FCSTD DOCUMENT  (FreeCAD 0.20R26155 (Git))
Label: C707 10M008 612 2
License: All rights reserved
LicenseURL: http://en.wikipedia.org/wiki/All_rights_reserved
objects: Sketcher::SketchObject×3
note: 3 computed .brp shape members not serialized (recipe doc carries the construction recipe); baked Part::Feature solids carry a one-line shape summary decoded from their .brp

FEATURE [Sketcher::SketchObject] Sketch  label="F_Silks_0.16"
  FullyConstrained = false
  MapMode = 5
  sketch-geometry (118):
    g0: LineSegment StartX=-3.32 StartY=-3.84 StartZ=0 EndX=-2.42 EndY=-3.84 EndZ=0
    g1: LineSegment StartX=-2.42 StartY=-3.84 StartZ=0 EndX=-2.42 EndY=-2.74 EndZ=0
    g2: LineSegment StartX=-2.42 StartY=-2.74 StartZ=0 EndX=-3.32 EndY=-2.74 EndZ=0
    g3: LineSegment StartX=-3.32 StartY=-2.74 StartZ=0 EndX=-3.32 EndY=-3.84 EndZ=0
    g4: LineSegment StartX=-3.32 StartY=-2.34 StartZ=0 EndX=-2.42 EndY=-2.34 EndZ=0
    g5: LineSegment StartX=-2.42 StartY=-2.34 StartZ=0 EndX=-2.42 EndY=-0.2 EndZ=0
    g6: LineSegment StartX=-2.42 StartY=-0.2 StartZ=0 EndX=-3.32 EndY=-0.2 EndZ=0
    g7: LineSegment StartX=-3.32 StartY=-0.2 StartZ=0 EndX=-3.32 EndY=-2.34 EndZ=0
    g8: LineSegment StartX=-3.32 StartY=-3.84 StartZ=0 EndX=-3.32 EndY=15.0884 EndZ=0
    g9: LineSegment StartX=2.42 StartY=-3.84 StartZ=0 EndX=3.32 EndY=-3.84 EndZ=0
    g10: LineSegment StartX=3.32 StartY=-3.84 StartZ=0 EndX=3.32 EndY=-2.74 EndZ=0
    g11: LineSegment StartX=3.32 StartY=-2.74 StartZ=0 EndX=2.42 EndY=-2.74 EndZ=0
    g12: LineSegment StartX=2.42 StartY=-2.74 StartZ=0 EndX=2.42 EndY=-3.84 EndZ=0
    g13: LineSegment StartX=2.42 StartY=-2.34 StartZ=0 EndX=3.32 EndY=-2.34 EndZ=0
    g14: LineSegment StartX=3.32 StartY=-2.34 StartZ=0 EndX=3.32 EndY=-0.2 EndZ=0
    g15: LineSegment StartX=3.32 StartY=-0.2 StartZ=0 EndX=2.42 EndY=-0.2 EndZ=0
    g16: LineSegment StartX=2.42 StartY=-0.2 StartZ=0 EndX=2.42 EndY=-2.34 EndZ=0
    g17: LineSegment StartX=-3.32 StartY=0.2 StartZ=0 EndX=-2.42 EndY=0.2 EndZ=0
    g18: LineSegment StartX=-2.42 StartY=0.2 StartZ=0 EndX=-2.42 EndY=2.34 EndZ=0
    g19: LineSegment StartX=-2.42 StartY=2.34 StartZ=0 EndX=-3.32 EndY=2.34 EndZ=0
    g20: LineSegment StartX=-3.32 StartY=2.34 StartZ=0 EndX=-3.32 EndY=0.2 EndZ=0
    g21: LineSegment StartX=2.42 StartY=0.2 StartZ=0 EndX=3.32 EndY=0.2 EndZ=0
    g22: LineSegment StartX=3.32 StartY=0.2 StartZ=0 EndX=3.32 EndY=2.34 EndZ=0
    g23: LineSegment StartX=3.32 StartY=2.34 StartZ=0 EndX=2.42 EndY=2.34 EndZ=0
    g24: LineSegment StartX=2.42 StartY=2.34 StartZ=0 EndX=2.42 EndY=0.2 EndZ=0
    g25: LineSegment StartX=2.42 StartY=-3.84 StartZ=0 EndX=2.42 EndY=14.9394 EndZ=0
    g26: LineSegment StartX=-3.32 StartY=2.74 StartZ=0 EndX=-2.42 EndY=2.74 EndZ=0
    g27: LineSegment StartX=-2.42 StartY=2.74 StartZ=0 EndX=-2.42 EndY=3.84 EndZ=0
    g28: LineSegment StartX=-2.42 StartY=3.84 StartZ=0 EndX=-3.32 EndY=3.84 EndZ=0
    g29: LineSegment StartX=-3.32 StartY=3.84 StartZ=0 EndX=-3.32 EndY=2.74 EndZ=0
    g30: LineSegment StartX=2.42 StartY=2.74 StartZ=0 EndX=3.32 EndY=2.74 EndZ=0
    g31: LineSegment StartX=3.32 StartY=2.74 StartZ=0 EndX=3.32 EndY=3.84 EndZ=0
    g32: LineSegment StartX=3.32 StartY=3.84 StartZ=0 EndX=2.42 EndY=3.84 EndZ=0
    g33: LineSegment StartX=2.42 StartY=3.84 StartZ=0 EndX=2.42 EndY=2.74 EndZ=0
    g34: LineSegment StartX=-4.32 StartY=5.13365 StartZ=0 EndX=-4.32 EndY=14.1961 EndZ=0
    g35: LineSegment StartX=3.62 StartY=5.28538 StartZ=0 EndX=3.62 EndY=13.9122 EndZ=0
    g36: LineSegment StartX=-4.32 StartY=-3.19 StartZ=0 EndX=-3.62 EndY=-3.19 EndZ=0
    g37: LineSegment StartX=-3.62 StartY=-3.19 StartZ=0 EndX=-3.62 EndY=-1.89 EndZ=0
    g38: LineSegment StartX=-3.62 StartY=-1.89 StartZ=0 EndX=-4.32 EndY=-1.89 EndZ=0
    g39: LineSegment StartX=-4.32 StartY=-1.89 StartZ=0 EndX=-4.32 EndY=-3.19 EndZ=0
    g40: LineSegment StartX=-4.32 StartY=-0.65 StartZ=0 EndX=-3.62 EndY=-0.65 EndZ=0
    g41: LineSegment StartX=-3.62 StartY=-0.65 StartZ=0 EndX=-3.62 EndY=0.65 EndZ=0
    g42: LineSegment StartX=-3.62 StartY=0.65 StartZ=0 EndX=-4.32 EndY=0.65 EndZ=0
    g43: LineSegment StartX=-4.32 StartY=0.65 StartZ=0 EndX=-4.32 EndY=-0.65 EndZ=0
    g44: LineSegment StartX=-4.32 StartY=1.89 StartZ=0 EndX=-3.62 EndY=1.89 EndZ=0
    g45: LineSegment StartX=-3.62 StartY=1.89 StartZ=0 EndX=-3.62 EndY=3.19 EndZ=0
    g46: LineSegment StartX=-3.62 StartY=3.19 StartZ=0 EndX=-4.32 EndY=3.19 EndZ=0
    g47: LineSegment StartX=-4.32 StartY=3.19 StartZ=0 EndX=-4.32 EndY=1.89 EndZ=0
    g48: LineSegment StartX=3.62 StartY=1.89 StartZ=0 EndX=4.32 EndY=1.89 EndZ=0
    g49: LineSegment StartX=4.32 StartY=1.89 StartZ=0 EndX=4.32 EndY=3.19 EndZ=0
    g50: LineSegment StartX=4.32 StartY=3.19 StartZ=0 EndX=3.62 EndY=3.19 EndZ=0
    g51: LineSegment StartX=3.62 StartY=3.19 StartZ=0 EndX=3.62 EndY=1.89 EndZ=0
    g52: LineSegment StartX=3.62 StartY=-0.65 StartZ=0 EndX=4.32 EndY=-0.65 EndZ=0
    g53: LineSegment StartX=4.32 StartY=-0.65 StartZ=0 EndX=4.32 EndY=0.65 EndZ=0
    g54: LineSegment StartX=4.32 StartY=0.65 StartZ=0 EndX=3.62 EndY=0.65 EndZ=0
    g55: LineSegment StartX=3.62 StartY=0.65 StartZ=0 EndX=3.62 EndY=-0.65 EndZ=0
    g56: LineSegment StartX=3.62 StartY=-3.19 StartZ=0 EndX=4.32 EndY=-3.19 EndZ=0
    g57: LineSegment StartX=4.32 StartY=-3.19 StartZ=0 EndX=4.32 EndY=-1.89 EndZ=0
    g58: LineSegment StartX=4.32 StartY=-1.89 StartZ=0 EndX=3.62 EndY=-1.89 EndZ=0
    g59: LineSegment StartX=3.62 StartY=-1.89 StartZ=0 EndX=3.62 EndY=-3.19 EndZ=0
    g60: LineSegment StartX=-2.42 StartY=-2.34 StartZ=0 EndX=2.42 EndY=-2.34 EndZ=0
    g61: LineSegment StartX=-2.42 StartY=0.2 StartZ=0 EndX=2.42 EndY=0.2 EndZ=0
    g62: LineSegment StartX=-2.42 StartY=2.74 StartZ=0 EndX=2.42 EndY=2.74 EndZ=0
    g63: LineSegment StartX=-2.42 StartY=-3.84 StartZ=0 EndX=2.42 EndY=-3.84 EndZ=0
    g64: LineSegment StartX=-3.62 StartY=-3.19 StartZ=0 EndX=3.62 EndY=-3.19 EndZ=0
    g65: LineSegment StartX=-3.62 StartY=-0.65 StartZ=0 EndX=3.62 EndY=-0.65 EndZ=0
    g66: LineSegment StartX=-3.62 StartY=1.89 StartZ=0 EndX=3.62 EndY=1.89 EndZ=0
    g67: LineSegment StartX=-0.9 StartY=-3.29 StartZ=0 EndX=-0.34 EndY=-3.29 EndZ=0
    g68: LineSegment StartX=-0.34 StartY=-3.29 StartZ=0 EndX=-0.34 EndY=-2.95 EndZ=0
    g69: LineSegment StartX=-0.34 StartY=-2.95 StartZ=0 EndX=-0.9 EndY=-2.95 EndZ=0
    g70: LineSegment StartX=-0.9 StartY=-2.95 StartZ=0 EndX=-0.9 EndY=-3.29 EndZ=0
    g71: LineSegment StartX=0.34 StartY=-3.29 StartZ=0 EndX=0.9 EndY=-3.29 EndZ=0
    g72: LineSegment StartX=0.9 StartY=-3.29 StartZ=0 EndX=0.9 EndY=-2.95 EndZ=0
    g73: LineSegment StartX=0.9 StartY=-2.95 StartZ=0 EndX=0.34 EndY=-2.95 EndZ=0
    g74: LineSegment StartX=0.34 StartY=-2.95 StartZ=0 EndX=0.34 EndY=-3.29 EndZ=0
    g75: LineSegment StartX=0.04 StartY=-2.31 StartZ=0 EndX=0.79 EndY=-2.31 EndZ=0
    g76: LineSegment StartX=0.79 StartY=-2.31 StartZ=0 EndX=0.79 EndY=-2.81 EndZ=0
    g77: LineSegment StartX=0.79 StartY=-2.81 StartZ=0 EndX=0.04 EndY=-2.81 EndZ=0
    g78: LineSegment StartX=0.04 StartY=-2.81 StartZ=0 EndX=0.04 EndY=-2.31 EndZ=0
    g79: LineSegment StartX=-0.79 StartY=-1.66 StartZ=0 EndX=-0.04 EndY=-1.66 EndZ=0
    g80: LineSegment StartX=-0.04 StartY=-1.66 StartZ=0 EndX=-0.04 EndY=-2.16 EndZ=0
    g81: LineSegment StartX=-0.04 StartY=-2.16 StartZ=0 EndX=-0.79 EndY=-2.16 EndZ=0
    g82: LineSegment StartX=-0.79 StartY=-2.16 StartZ=0 EndX=-0.79 EndY=-1.66 EndZ=0
    g83: LineSegment StartX=0.04 StartY=-1.07 StartZ=0 EndX=0.79 EndY=-1.07 EndZ=0
    g84: LineSegment StartX=0.79 StartY=-1.07 StartZ=0 EndX=0.79 EndY=-0.57 EndZ=0
    g85: LineSegment StartX=0.79 StartY=-0.57 StartZ=0 EndX=0.04 EndY=-0.57 EndZ=0
    g86: LineSegment StartX=0.04 StartY=-0.57 StartZ=0 EndX=0.04 EndY=-1.07 EndZ=0
    g87: LineSegment StartX=-0.79 StartY=1.07 StartZ=0 EndX=-0.04 EndY=1.07 EndZ=0
    g88: LineSegment StartX=-0.04 StartY=1.07 StartZ=0 EndX=-0.04 EndY=0.57 EndZ=0
    g89: LineSegment StartX=-0.04 StartY=0.57 StartZ=0 EndX=-0.79 EndY=0.57 EndZ=0
    g90: LineSegment StartX=-0.79 StartY=0.57 StartZ=0 EndX=-0.79 EndY=1.07 EndZ=0
    g91: LineSegment StartX=0.04 StartY=1.66 StartZ=0 EndX=0.79 EndY=1.66 EndZ=0
    g92: LineSegment StartX=0.79 StartY=1.66 StartZ=0 EndX=0.79 EndY=2.16 EndZ=0
    g93: LineSegment StartX=0.79 StartY=2.16 StartZ=0 EndX=0.04 EndY=2.16 EndZ=0
    g94: LineSegment StartX=0.04 StartY=2.16 StartZ=0 EndX=0.04 EndY=1.66 EndZ=0
    g95: LineSegment StartX=-0.79 StartY=2.81 StartZ=0 EndX=-0.04 EndY=2.81 EndZ=0
    g96: LineSegment StartX=-0.04 StartY=2.81 StartZ=0 EndX=-0.04 EndY=2.31 EndZ=0
    g97: LineSegment StartX=-0.04 StartY=2.31 StartZ=0 EndX=-0.79 EndY=2.31 EndZ=0
    g98: LineSegment StartX=-0.79 StartY=2.31 StartZ=0 EndX=-0.79 EndY=2.81 EndZ=0
    g99: LineSegment StartX=0.34 StartY=3.29 StartZ=0 EndX=0.9 EndY=3.29 EndZ=0
    g100: LineSegment StartX=0.9 StartY=3.29 StartZ=0 EndX=0.9 EndY=2.95 EndZ=0
    g101: LineSegment StartX=0.9 StartY=2.95 StartZ=0 EndX=0.34 EndY=2.95 EndZ=0
    g102: LineSegment StartX=0.34 StartY=2.95 StartZ=0 EndX=0.34 EndY=3.29 EndZ=0
    g103: LineSegment StartX=-0.9 StartY=3.29 StartZ=0 EndX=-0.34 EndY=3.29 EndZ=0
    g104: LineSegment StartX=-0.34 StartY=3.29 StartZ=0 EndX=-0.34 EndY=2.95 EndZ=0
    g105: LineSegment StartX=-0.34 StartY=2.95 StartZ=0 EndX=-0.9 EndY=2.95 EndZ=0
    g106: LineSegment StartX=-0.9 StartY=2.95 StartZ=0 EndX=-0.9 EndY=3.29 EndZ=0
    g107: LineSegment StartX=-0.9 StartY=2.95 StartZ=0 EndX=-0.9 EndY=5.53187 EndZ=0
    g108: LineSegment StartX=-0.79 StartY=2.31 StartZ=0 EndX=-0.79 EndY=5.36472 EndZ=0
    g109: LineSegment StartX=0.04 StartY=1.66 StartZ=0 EndX=0.04 EndY=5.08492 EndZ=0
    g110: LineSegment StartX=0.34 StartY=2.95 StartZ=0 EndX=0.34 EndY=3.02051 EndZ=0
    g111: LineSegment StartX=-0.34 StartY=2.95 StartZ=0 EndX=0.34 EndY=2.95 EndZ=0
    g112: LineSegment StartX=-0.34 StartY=-3.29 StartZ=0 EndX=0.34 EndY=-3.29 EndZ=0
    g113: LineSegment StartX=4.32 StartY=-3.84 StartZ=0 EndX=4.32 EndY=3.84 EndZ=0
    g114: LineSegment StartX=4.32 StartY=3.84 StartZ=0 EndX=-4.32 EndY=3.84 EndZ=0
    g115: LineSegment StartX=-4.32 StartY=3.84 StartZ=0 EndX=-4.32 EndY=-3.84 EndZ=0
    g116: LineSegment StartX=-4.32 StartY=-3.84 StartZ=0 EndX=4.32 EndY=-3.84 EndZ=0
    g117: GeomPoint X=0 Y=0 Z=0
  constraints (334):
    c: Coincident(g0,g1)
    c: Coincident(g1,g2)
    c: Coincident(g2,g3)
    c: Coincident(g3,g0)
    c: Horizontal(g0)
    c: Horizontal(g2)
    c: Vertical(g1)
    c: Vertical(g3)
    c: DistanceX(g2,g2) = 0.9
    c: Coincident(g4,g5)
    c: Coincident(g5,g6)
    c: Coincident(g6,g7)
    c: Coincident(g7,g4)
    c: Horizontal(g4)
    c: Horizontal(g6)
    c: Vertical(g5)
    c: Vertical(g7)
    c: Coincident(g8,g0)
    c: Vertical(g8)
    c: PointOnObject(g4,g8)
    c: DistanceY(g0,g4) = 1.5
    c: Coincident(g9,g10)
    c: Coincident(g10,g11)
    c: Coincident(g11,g12)
    c: Coincident(g12,g9)
    c: Horizontal(g9)
    c: Horizontal(g11)
    c: Vertical(g10)
    c: Vertical(g12)
    c: Coincident(g13,g14)
    c: Coincident(g14,g15)
    c: Coincident(g15,g16)
    c: Coincident(g16,g13)
    c: Horizontal(g13)
    c: Horizontal(g15)
    c: Vertical(g14)
    c: Vertical(g16)
    c: Coincident(g17,g18)
    c: Coincident(g18,g19)
    c: Coincident(g19,g20)
    c: Coincident(g20,g17)
    c: Horizontal(g17)
    c: Horizontal(g19)
    c: Vertical(g18)
    c: Vertical(g20)
    c: PointOnObject(g17,g8)
    c: Coincident(g21,g22)
    c: Coincident(g22,g23)
    c: Coincident(g23,g24)
    c: Coincident(g24,g21)
    c: Horizontal(g21)
    c: Horizontal(g23)
    c: Vertical(g22)
    c: Vertical(g24)
    c: Coincident(g25,g9)
    c: Vertical(g25)
    c: PointOnObject(g23,g25)
    c: PointOnObject(g15,g25)
    c: DistanceY(g0,g17) = 4.04
    c: DistanceX(g8,g25) = 5.74
    c: Coincident(g26,g27)
    c: Coincident(g27,g28)
    c: Coincident(g28,g29)
    c: Coincident(g29,g26)
    c: Horizontal(g26)
    c: Horizontal(g28)
    c: Vertical(g27)
    c: Vertical(g29)
    c: PointOnObject(g26,g8)
    c: Coincident(g30,g31)
    c: Coincident(g31,g32)
    c: Coincident(g32,g33)
    c: Coincident(g33,g30)
    c: Horizontal(g30)
    c: Horizontal(g32)
    c: Vertical(g31)
    c: Vertical(g33)
    c: PointOnObject(g30,g25)
    c: Equal(g2,g6)
    c: Equal(g6,g19)
    c: Equal(g19,g28)
    c: Equal(g28,g32)
    c: Equal(g32,g23)
    c: Equal(g23,g15)
    c: Equal(g15,g11)
    c: Equal(g5,g18)
    c: Equal(g18,g24)
    c: Equal(g24,g16)
    c: DistanceY(g7,g7) = 2.14
    c: Equal(g1,g12)
    c: Equal(g12,g33)
    c: Equal(g33,g27)
    c: Vertical(g34)
    c: Vertical(g35)
    c: Coincident(g36,g37)
    c: Coincident(g37,g38)
    c: Coincident(g38,g39)
    c: Coincident(g39,g36)
    c: Horizontal(g36)
    c: Horizontal(g38)
    c: Vertical(g37)
    c: Vertical(g39)
    c: PointOnObject(g36,g34)
    c: Coincident(g40,g41)
    c: Coincident(g41,g42)
    c: Coincident(g42,g43)
    c: Coincident(g43,g40)
    c: Horizontal(g40)
    c: Horizontal(g42)
    c: Vertical(g41)
    c: Vertical(g43)
    c: PointOnObject(g40,g34)
    c: Coincident(g44,g45)
    c: Coincident(g45,g46)
    c: Coincident(g46,g47)
    c: Coincident(g47,g44)
    c: Horizontal(g44)
    c: Horizontal(g46)
    c: Vertical(g45)
    c: Vertical(g47)
    c: PointOnObject(g44,g34)
    c: Coincident(g48,g49)
    c: Coincident(g49,g50)
    c: Coincident(g50,g51)
    c: Coincident(g51,g48)
    c: Horizontal(g48)
    c: Horizontal(g50)
    c: Vertical(g49)
    c: Vertical(g51)
    c: PointOnObject(g48,g35)
    c: Coincident(g52,g53)
    c: Coincident(g53,g54)
    c: Coincident(g54,g55)
    c: Coincident(g55,g52)
    c: Horizontal(g52)
    c: Horizontal(g54)
    c: Vertical(g53)
    c: Vertical(g55)
    c: PointOnObject(g52,g35)
    c: Coincident(g56,g57)
    c: Coincident(g57,g58)
    c: Coincident(g58,g59)
    c: Coincident(g59,g56)
    c: Horizontal(g56)
    c: Horizontal(g58)
    c: Vertical(g57)
    c: Vertical(g59)
    c: PointOnObject(g56,g35)
    c: DistanceX(g34,g8) = 1
    c: Equal(g38,g42)
    c: Equal(g42,g46)
    c: Equal(g46,g50)
    c: Equal(g50,g54)
    c: Equal(g54,g56)
    c: Equal(g41,g45)
    c: Equal(g45,g37)
    c: Equal(g37,g57)
    c: Equal(g57,g53)
    c: Equal(g53,g49)
    c: DistanceX(g50,g50) = 0.7
    c: DistanceY(g49,g49) = 1.3
    c: Coincident(g60,g4)
    c: Coincident(g60,g13)
    c: Horizontal(g60)
    c: Coincident(g61,g17)
    c: Coincident(g61,g21)
    c: Horizontal(g61)
    c: Coincident(g62,g26)
    c: Coincident(g62,g30)
    c: Horizontal(g62)
    c: DistanceY(g0,g26) = 6.58
    c: DistanceY(g10,g10) = 1.1
    c: Coincident(g63,g0)
    c: Coincident(g63,g9)
    c: Horizontal(g63)
    c: Coincident(g64,g36)
    c: Coincident(g64,g56)
    c: Coincident(g65,g40)
    c: Coincident(g65,g52)
    c: Coincident(g66,g44)
    c: Coincident(g66,g48)
    c: Horizontal(g66)
    c: Horizontal(g65)
    c: Horizontal(g64)
    c: DistanceY(g0,g36) = 0.65
    c: DistanceY(g0,g40) = 3.19
    c: DistanceY(g0,g44) = 5.73
    c: DistanceX(g0,g35) = 6.94
    c: Coincident(g67,g68)
    c: Coincident(g68,g69)
    c: Coincident(g69,g70)
    c: Coincident(g70,g67)
    c: Horizontal(g67)
    c: Horizontal(g69)
    c: Vertical(g68)
    c: Vertical(g70)
    c: Coincident(g71,g72)
    c: Coincident(g72,g73)
    c: Coincident(g73,g74)
    c: Coincident(g74,g71)
    c: Horizontal(g71)
    c: Horizontal(g73)
    c: Vertical(g72)
    c: Vertical(g74)
    c: Coincident(g75,g76)
    c: Coincident(g76,g77)
    c: Coincident(g77,g78)
    c: Coincident(g78,g75)
    c: Horizontal(g75)
    c: Horizontal(g77)
    c: Vertical(g76)
    c: Vertical(g78)
    c: Coincident(g79,g80)
    c: Coincident(g80,g81)
    c: Coincident(g81,g82)
    c: Coincident(g82,g79)
    c: Horizontal(g79)
    c: Horizontal(g81)
    c: Vertical(g80)
    c: Vertical(g82)
    c: Coincident(g83,g84)
    c: Coincident(g84,g85)
    c: Coincident(g85,g86)
    c: Coincident(g86,g83)
    c: Horizontal(g83)
    c: Horizontal(g85)
    c: Vertical(g84)
    c: Vertical(g86)
    c: Coincident(g87,g88)
    c: Coincident(g88,g89)
    c: Coincident(g89,g90)
    c: Coincident(g90,g87)
    c: Horizontal(g87)
    c: Horizontal(g89)
    c: Vertical(g88)
    c: Vertical(g90)
    c: Coincident(g91,g92)
    c: Coincident(g92,g93)
    c: Coincident(g93,g94)
    c: Coincident(g94,g91)
    c: Horizontal(g91)
    c: Horizontal(g93)
    c: Vertical(g92)
    c: Vertical(g94)
    c: Coincident(g95,g96)
    c: Coincident(g96,g97)
    c: Coincident(g97,g98)
    c: Coincident(g98,g95)
    c: Horizontal(g95)
    c: Horizontal(g97)
    c: Vertical(g96)
    c: Vertical(g98)
    c: Coincident(g99,g100)
    c: Coincident(g100,g101)
    c: Coincident(g101,g102)
    c: Coincident(g102,g99)
    c: Horizontal(g99)
    c: Horizontal(g101)
    c: Vertical(g100)
    c: Vertical(g102)
    c: Coincident(g103,g104)
    c: Coincident(g104,g105)
    c: Coincident(g105,g106)
    c: Coincident(g106,g103)
    c: Horizontal(g103)
    c: Horizontal(g105)
    c: Vertical(g104)
    c: Vertical(g106)
    c: Coincident(g107,g105)
    c: Vertical(g107)
    c: Coincident(g108,g97)
    c: Vertical(g108)
    c: Coincident(g109,g91)
    c: Vertical(g109)
    c: Equal(g67,g71)
    c: Equal(g71,g105)
    c: Equal(g105,g101)
    c: Equal(g100,g104)
    c: Equal(g104,g72)
    c: Equal(g72,g68)
    c: Equal(g96,g94)
    c: Equal(g94,g88)
    c: Equal(g88,g86)
    c: Equal(g86,g80)
    c: Equal(g80,g78)
    c: Equal(g77,g81)
    c: Equal(g81,g83)
    c: Equal(g83,g89)
    c: Equal(g89,g91)
    c: Equal(g91,g97)
    c: PointOnObject(g83,g109)
    c: PointOnObject(g77,g109)
    c: PointOnObject(g87,g108)
    c: PointOnObject(g79,g108)
    c: Coincident(g110,g101)
    c: Vertical(g110)
    c: PointOnObject(g71,g110)
    c: DistanceX(g103,g103) = 0.56
    c: DistanceX(g95,g95) = 0.75
    c: DistanceY(g96,g96) = 0.5
    c: PointOnObject(g67,g107)
    c: DistanceX(g0,g107) = 2.42
    c: DistanceX(g0,g108) = 2.53
    c: DistanceX(g0,g109) = 3.36
    c: DistanceX(g0,g110) = 3.66
    c: Coincident(g111,g104)
    c: Coincident(g111,g101)
    c: Coincident(g112,g67)
    c: Coincident(g112,g71)
    c: Horizontal(g112)
    c: Horizontal(g111)
    c: DistanceY(g0,g67) = 0.55
    c: DistanceY(g0,g105) = 6.79
    c: DistanceY(g100,g100) = 0.34
    c: DistanceY(g0,g77) = 1.03
    c: DistanceY(g0,g81) = 1.68
    c: DistanceY(g0,g83) = 2.77
    c: DistanceY(g0,g89) = 4.41
    c: DistanceY(g0,g91) = 5.5
    c: DistanceY(g0,g97) = 6.15
    c: Coincident(g113,g114)
    c: Coincident(g114,g115)
    c: Coincident(g115,g116)
    c: Coincident(g116,g113)
    c: Horizontal(g114)
    c: Horizontal(g116)
    c: Vertical(g113)
    c: Vertical(g115)
    c: Symmetric(g114,g113,g117)
    c: Coincident(g117,g-1)
    c: PointOnObject(g28,g114)
    c: PointOnObject(g46,g115)
    c: PointOnObject(g48,g113)
    c: PointOnObject(g9,g116)
FEATURE [Sketcher::SketchObject] Sketch001  label="F_CrtYd_0.05"
  FullyConstrained = true
  MapMode = 5
  sketch-geometry (5):
    g0: LineSegment StartX=-4.5 StartY=-4 StartZ=0 EndX=-4.5 EndY=4 EndZ=0
    g1: LineSegment StartX=-4.5 StartY=4 StartZ=0 EndX=4.5 EndY=4 EndZ=0
    g2: LineSegment StartX=4.5 StartY=4 StartZ=0 EndX=4.5 EndY=-4 EndZ=0
    g3: LineSegment StartX=4.5 StartY=-4 StartZ=0 EndX=-4.5 EndY=-4 EndZ=0
    g4: GeomPoint X=0 Y=0 Z=0
  constraints (12):
    c: Coincident(g0,g1)
    c: Coincident(g1,g2)
    c: Coincident(g2,g3)
    c: Coincident(g3,g0)
    c: Horizontal(g1)
    c: Horizontal(g3)
    c: Vertical(g0)
    c: Vertical(g2)
    c: Symmetric(g1,g0,g4)
    c: Coincident(g4,g-1)
    c: DistanceY(g2,g2) = 8
    c: DistanceX(g1,g1) = 9
FEATURE [Sketcher::SketchObject] Sketch002  label="Pads_TH_SMD"
  FullyConstrained = false
  MapMode = 5
  sketch-geometry (118):
    g0: LineSegment StartX=-3.32 StartY=-3.84 StartZ=0 EndX=-2.42 EndY=-3.84 EndZ=0
    g1: LineSegment StartX=-2.42 StartY=-3.84 StartZ=0 EndX=-2.42 EndY=-2.74 EndZ=0
    g2: LineSegment StartX=-2.42 StartY=-2.74 StartZ=0 EndX=-3.32 EndY=-2.74 EndZ=0
    g3: LineSegment StartX=-3.32 StartY=-2.74 StartZ=0 EndX=-3.32 EndY=-3.84 EndZ=0
    g4: LineSegment StartX=-3.32 StartY=-2.34 StartZ=0 EndX=-2.42 EndY=-2.34 EndZ=0
    g5: LineSegment StartX=-2.42 StartY=-2.34 StartZ=0 EndX=-2.42 EndY=-0.2 EndZ=0
    g6: LineSegment StartX=-2.42 StartY=-0.2 StartZ=0 EndX=-3.32 EndY=-0.2 EndZ=0
    g7: LineSegment StartX=-3.32 StartY=-0.2 StartZ=0 EndX=-3.32 EndY=-2.34 EndZ=0
    g8: LineSegment StartX=-3.32 StartY=-3.84 StartZ=0 EndX=-3.32 EndY=15.0884 EndZ=0
    g9: LineSegment StartX=2.42 StartY=-3.84 StartZ=0 EndX=3.32 EndY=-3.84 EndZ=0
    g10: LineSegment StartX=3.32 StartY=-3.84 StartZ=0 EndX=3.32 EndY=-2.74 EndZ=0
    g11: LineSegment StartX=3.32 StartY=-2.74 StartZ=0 EndX=2.42 EndY=-2.74 EndZ=0
    g12: LineSegment StartX=2.42 StartY=-2.74 StartZ=0 EndX=2.42 EndY=-3.84 EndZ=0
    g13: LineSegment StartX=2.42 StartY=-2.34 StartZ=0 EndX=3.32 EndY=-2.34 EndZ=0
    g14: LineSegment StartX=3.32 StartY=-2.34 StartZ=0 EndX=3.32 EndY=-0.2 EndZ=0
    g15: LineSegment StartX=3.32 StartY=-0.2 StartZ=0 EndX=2.42 EndY=-0.2 EndZ=0
    g16: LineSegment StartX=2.42 StartY=-0.2 StartZ=0 EndX=2.42 EndY=-2.34 EndZ=0
    g17: LineSegment StartX=-3.32 StartY=0.2 StartZ=0 EndX=-2.42 EndY=0.2 EndZ=0
    g18: LineSegment StartX=-2.42 StartY=0.2 StartZ=0 EndX=-2.42 EndY=2.34 EndZ=0
    g19: LineSegment StartX=-2.42 StartY=2.34 StartZ=0 EndX=-3.32 EndY=2.34 EndZ=0
    g20: LineSegment StartX=-3.32 StartY=2.34 StartZ=0 EndX=-3.32 EndY=0.2 EndZ=0
    g21: LineSegment StartX=2.42 StartY=0.2 StartZ=0 EndX=3.32 EndY=0.2 EndZ=0
    g22: LineSegment StartX=3.32 StartY=0.2 StartZ=0 EndX=3.32 EndY=2.34 EndZ=0
    g23: LineSegment StartX=3.32 StartY=2.34 StartZ=0 EndX=2.42 EndY=2.34 EndZ=0
    g24: LineSegment StartX=2.42 StartY=2.34 StartZ=0 EndX=2.42 EndY=0.2 EndZ=0
    g25: LineSegment StartX=2.42 StartY=-3.84 StartZ=0 EndX=2.42 EndY=14.9394 EndZ=0
    g26: LineSegment StartX=-3.32 StartY=2.74 StartZ=0 EndX=-2.42 EndY=2.74 EndZ=0
    g27: LineSegment StartX=-2.42 StartY=2.74 StartZ=0 EndX=-2.42 EndY=3.84 EndZ=0
    g28: LineSegment StartX=-2.42 StartY=3.84 StartZ=0 EndX=-3.32 EndY=3.84 EndZ=0
    g29: LineSegment StartX=-3.32 StartY=3.84 StartZ=0 EndX=-3.32 EndY=2.74 EndZ=0
    g30: LineSegment StartX=2.42 StartY=2.74 StartZ=0 EndX=3.32 EndY=2.74 EndZ=0
    g31: LineSegment StartX=3.32 StartY=2.74 StartZ=0 EndX=3.32 EndY=3.84 EndZ=0
    g32: LineSegment StartX=3.32 StartY=3.84 StartZ=0 EndX=2.42 EndY=3.84 EndZ=0
    g33: LineSegment StartX=2.42 StartY=3.84 StartZ=0 EndX=2.42 EndY=2.74 EndZ=0
    g34: LineSegment StartX=-4.32 StartY=5.13365 StartZ=0 EndX=-4.32 EndY=14.1961 EndZ=0
    g35: LineSegment StartX=3.62 StartY=5.28538 StartZ=0 EndX=3.62 EndY=13.9122 EndZ=0
    g36: LineSegment StartX=-4.32 StartY=-3.19 StartZ=0 EndX=-3.62 EndY=-3.19 EndZ=0
    g37: LineSegment StartX=-3.62 StartY=-3.19 StartZ=0 EndX=-3.62 EndY=-1.89 EndZ=0
    g38: LineSegment StartX=-3.62 StartY=-1.89 StartZ=0 EndX=-4.32 EndY=-1.89 EndZ=0
    g39: LineSegment StartX=-4.32 StartY=-1.89 StartZ=0 EndX=-4.32 EndY=-3.19 EndZ=0
    g40: LineSegment StartX=-4.32 StartY=-0.65 StartZ=0 EndX=-3.62 EndY=-0.65 EndZ=0
    g41: LineSegment StartX=-3.62 StartY=-0.65 StartZ=0 EndX=-3.62 EndY=0.65 EndZ=0
    g42: LineSegment StartX=-3.62 StartY=0.65 StartZ=0 EndX=-4.32 EndY=0.65 EndZ=0
    g43: LineSegment StartX=-4.32 StartY=0.65 StartZ=0 EndX=-4.32 EndY=-0.65 EndZ=0
    g44: LineSegment StartX=-4.32 StartY=1.89 StartZ=0 EndX=-3.62 EndY=1.89 EndZ=0
    g45: LineSegment StartX=-3.62 StartY=1.89 StartZ=0 EndX=-3.62 EndY=3.19 EndZ=0
    g46: LineSegment StartX=-3.62 StartY=3.19 StartZ=0 EndX=-4.32 EndY=3.19 EndZ=0
    g47: LineSegment StartX=-4.32 StartY=3.19 StartZ=0 EndX=-4.32 EndY=1.89 EndZ=0
    g48: LineSegment StartX=3.62 StartY=1.89 StartZ=0 EndX=4.32 EndY=1.89 EndZ=0
    g49: LineSegment StartX=4.32 StartY=1.89 StartZ=0 EndX=4.32 EndY=3.19 EndZ=0
    g50: LineSegment StartX=4.32 StartY=3.19 StartZ=0 EndX=3.62 EndY=3.19 EndZ=0
    g51: LineSegment StartX=3.62 StartY=3.19 StartZ=0 EndX=3.62 EndY=1.89 EndZ=0
    g52: LineSegment StartX=3.62 StartY=-0.65 StartZ=0 EndX=4.32 EndY=-0.65 EndZ=0
    g53: LineSegment StartX=4.32 StartY=-0.65 StartZ=0 EndX=4.32 EndY=0.65 EndZ=0
    g54: LineSegment StartX=4.32 StartY=0.65 StartZ=0 EndX=3.62 EndY=0.65 EndZ=0
    g55: LineSegment StartX=3.62 StartY=0.65 StartZ=0 EndX=3.62 EndY=-0.65 EndZ=0
    g56: LineSegment StartX=3.62 StartY=-3.19 StartZ=0 EndX=4.32 EndY=-3.19 EndZ=0
    g57: LineSegment StartX=4.32 StartY=-3.19 StartZ=0 EndX=4.32 EndY=-1.89 EndZ=0
    g58: LineSegment StartX=4.32 StartY=-1.89 StartZ=0 EndX=3.62 EndY=-1.89 EndZ=0
    g59: LineSegment StartX=3.62 StartY=-1.89 StartZ=0 EndX=3.62 EndY=-3.19 EndZ=0
    g60: LineSegment StartX=-2.42 StartY=-2.34 StartZ=0 EndX=2.42 EndY=-2.34 EndZ=0
    g61: LineSegment StartX=-2.42 StartY=0.2 StartZ=0 EndX=2.42 EndY=0.2 EndZ=0
    g62: LineSegment StartX=-2.42 StartY=2.74 StartZ=0 EndX=2.42 EndY=2.74 EndZ=0
    g63: LineSegment StartX=-2.42 StartY=-3.84 StartZ=0 EndX=2.42 EndY=-3.84 EndZ=0
    g64: LineSegment StartX=-3.62 StartY=-3.19 StartZ=0 EndX=3.62 EndY=-3.19 EndZ=0
    g65: LineSegment StartX=-3.62 StartY=-0.65 StartZ=0 EndX=3.62 EndY=-0.65 EndZ=0
    g66: LineSegment StartX=-3.62 StartY=1.89 StartZ=0 EndX=3.62 EndY=1.89 EndZ=0
    g67: LineSegment StartX=-0.9 StartY=-3.29 StartZ=0 EndX=-0.34 EndY=-3.29 EndZ=0
    g68: LineSegment StartX=-0.34 StartY=-3.29 StartZ=0 EndX=-0.34 EndY=-2.95 EndZ=0
    g69: LineSegment StartX=-0.34 StartY=-2.95 StartZ=0 EndX=-0.9 EndY=-2.95 EndZ=0
    g70: LineSegment StartX=-0.9 StartY=-2.95 StartZ=0 EndX=-0.9 EndY=-3.29 EndZ=0
    g71: LineSegment StartX=0.34 StartY=-3.29 StartZ=0 EndX=0.9 EndY=-3.29 EndZ=0
    g72: LineSegment StartX=0.9 StartY=-3.29 StartZ=0 EndX=0.9 EndY=-2.95 EndZ=0
    g73: LineSegment StartX=0.9 StartY=-2.95 StartZ=0 EndX=0.34 EndY=-2.95 EndZ=0
    g74: LineSegment StartX=0.34 StartY=-2.95 StartZ=0 EndX=0.34 EndY=-3.29 EndZ=0
    g75: LineSegment StartX=0.04 StartY=-2.31 StartZ=0 EndX=0.79 EndY=-2.31 EndZ=0
    g76: LineSegment StartX=0.79 StartY=-2.31 StartZ=0 EndX=0.79 EndY=-2.81 EndZ=0
    g77: LineSegment StartX=0.79 StartY=-2.81 StartZ=0 EndX=0.04 EndY=-2.81 EndZ=0
    g78: LineSegment StartX=0.04 StartY=-2.81 StartZ=0 EndX=0.04 EndY=-2.31 EndZ=0
    g79: LineSegment StartX=-0.79 StartY=-1.66 StartZ=0 EndX=-0.04 EndY=-1.66 EndZ=0
    g80: LineSegment StartX=-0.04 StartY=-1.66 StartZ=0 EndX=-0.04 EndY=-2.16 EndZ=0
    g81: LineSegment StartX=-0.04 StartY=-2.16 StartZ=0 EndX=-0.79 EndY=-2.16 EndZ=0
    g82: LineSegment StartX=-0.79 StartY=-2.16 StartZ=0 EndX=-0.79 EndY=-1.66 EndZ=0
    g83: LineSegment StartX=0.04 StartY=-1.07 StartZ=0 EndX=0.79 EndY=-1.07 EndZ=0
    g84: LineSegment StartX=0.79 StartY=-1.07 StartZ=0 EndX=0.79 EndY=-0.57 EndZ=0
    g85: LineSegment StartX=0.79 StartY=-0.57 StartZ=0 EndX=0.04 EndY=-0.57 EndZ=0
    g86: LineSegment StartX=0.04 StartY=-0.57 StartZ=0 EndX=0.04 EndY=-1.07 EndZ=0
    g87: LineSegment StartX=-0.79 StartY=1.07 StartZ=0 EndX=-0.04 EndY=1.07 EndZ=0
    g88: LineSegment StartX=-0.04 StartY=1.07 StartZ=0 EndX=-0.04 EndY=0.57 EndZ=0
    g89: LineSegment StartX=-0.04 StartY=0.57 StartZ=0 EndX=-0.79 EndY=0.57 EndZ=0
    g90: LineSegment StartX=-0.79 StartY=0.57 StartZ=0 EndX=-0.79 EndY=1.07 EndZ=0
    g91: LineSegment StartX=0.04 StartY=1.66 StartZ=0 EndX=0.79 EndY=1.66 EndZ=0
    g92: LineSegment StartX=0.79 StartY=1.66 StartZ=0 EndX=0.79 EndY=2.16 EndZ=0
    g93: LineSegment StartX=0.79 StartY=2.16 StartZ=0 EndX=0.04 EndY=2.16 EndZ=0
    g94: LineSegment StartX=0.04 StartY=2.16 StartZ=0 EndX=0.04 EndY=1.66 EndZ=0
    g95: LineSegment StartX=-0.79 StartY=2.81 StartZ=0 EndX=-0.04 EndY=2.81 EndZ=0
    g96: LineSegment StartX=-0.04 StartY=2.81 StartZ=0 EndX=-0.04 EndY=2.31 EndZ=0
    g97: LineSegment StartX=-0.04 StartY=2.31 StartZ=0 EndX=-0.79 EndY=2.31 EndZ=0
    g98: LineSegment StartX=-0.79 StartY=2.31 StartZ=0 EndX=-0.79 EndY=2.81 EndZ=0
    g99: LineSegment StartX=0.34 StartY=3.29 StartZ=0 EndX=0.9 EndY=3.29 EndZ=0
    g100: LineSegment StartX=0.9 StartY=3.29 StartZ=0 EndX=0.9 EndY=2.95 EndZ=0
    g101: LineSegment StartX=0.9 StartY=2.95 StartZ=0 EndX=0.34 EndY=2.95 EndZ=0
    g102: LineSegment StartX=0.34 StartY=2.95 StartZ=0 EndX=0.34 EndY=3.29 EndZ=0
    g103: LineSegment StartX=-0.9 StartY=3.29 StartZ=0 EndX=-0.34 EndY=3.29 EndZ=0
    g104: LineSegment StartX=-0.34 StartY=3.29 StartZ=0 EndX=-0.34 EndY=2.95 EndZ=0
    g105: LineSegment StartX=-0.34 StartY=2.95 StartZ=0 EndX=-0.9 EndY=2.95 EndZ=0
    g106: LineSegment StartX=-0.9 StartY=2.95 StartZ=0 EndX=-0.9 EndY=3.29 EndZ=0
    g107: LineSegment StartX=-0.9 StartY=2.95 StartZ=0 EndX=-0.9 EndY=5.53187 EndZ=0
    g108: LineSegment StartX=-0.79 StartY=2.31 StartZ=0 EndX=-0.79 EndY=5.36472 EndZ=0
    g109: LineSegment StartX=0.04 StartY=1.66 StartZ=0 EndX=0.04 EndY=5.08492 EndZ=0
    g110: LineSegment StartX=0.34 StartY=2.95 StartZ=0 EndX=0.34 EndY=3.02051 EndZ=0
    g111: LineSegment StartX=-0.34 StartY=2.95 StartZ=0 EndX=0.34 EndY=2.95 EndZ=0
    g112: LineSegment StartX=-0.34 StartY=-3.29 StartZ=0 EndX=0.34 EndY=-3.29 EndZ=0
    g113: LineSegment StartX=4.32 StartY=-3.84 StartZ=0 EndX=4.32 EndY=3.84 EndZ=0
    g114: LineSegment StartX=4.32 StartY=3.84 StartZ=0 EndX=-4.32 EndY=3.84 EndZ=0
    g115: LineSegment StartX=-4.32 StartY=3.84 StartZ=0 EndX=-4.32 EndY=-3.84 EndZ=0
    g116: LineSegment StartX=-4.32 StartY=-3.84 StartZ=0 EndX=4.32 EndY=-3.84 EndZ=0
    g117: GeomPoint X=0 Y=0 Z=0
  constraints (334):
    c: Coincident(g0,g1)
    c: Coincident(g1,g2)
    c: Coincident(g2,g3)
    c: Coincident(g3,g0)
    c: Horizontal(g0)
    c: Horizontal(g2)
    c: Vertical(g1)
    c: Vertical(g3)
    c: DistanceX(g2,g2) = 0.9
    c: Coincident(g4,g5)
    c: Coincident(g5,g6)
    c: Coincident(g6,g7)
    c: Coincident(g7,g4)
    c: Horizontal(g4)
    c: Horizontal(g6)
    c: Vertical(g5)
    c: Vertical(g7)
    c: Coincident(g8,g0)
    c: Vertical(g8)
    c: PointOnObject(g4,g8)
    c: DistanceY(g0,g4) = 1.5
    c: Coincident(g9,g10)
    c: Coincident(g10,g11)
    c: Coincident(g11,g12)
    c: Coincident(g12,g9)
    c: Horizontal(g9)
    c: Horizontal(g11)
    c: Vertical(g10)
    c: Vertical(g12)
    c: Coincident(g13,g14)
    c: Coincident(g14,g15)
    c: Coincident(g15,g16)
    c: Coincident(g16,g13)
    c: Horizontal(g13)
    c: Horizontal(g15)
    c: Vertical(g14)
    c: Vertical(g16)
    c: Coincident(g17,g18)
    c: Coincident(g18,g19)
    c: Coincident(g19,g20)
    c: Coincident(g20,g17)
    c: Horizontal(g17)
    c: Horizontal(g19)
    c: Vertical(g18)
    c: Vertical(g20)
    c: PointOnObject(g17,g8)
    c: Coincident(g21,g22)
    c: Coincident(g22,g23)
    c: Coincident(g23,g24)
    c: Coincident(g24,g21)
    c: Horizontal(g21)
    c: Horizontal(g23)
    c: Vertical(g22)
    c: Vertical(g24)
    c: Coincident(g25,g9)
    c: Vertical(g25)
    c: PointOnObject(g23,g25)
    c: PointOnObject(g15,g25)
    c: DistanceY(g0,g17) = 4.04
    c: DistanceX(g8,g25) = 5.74
    c: Coincident(g26,g27)
    c: Coincident(g27,g28)
    c: Coincident(g28,g29)
    c: Coincident(g29,g26)
    c: Horizontal(g26)
    c: Horizontal(g28)
    c: Vertical(g27)
    c: Vertical(g29)
    c: PointOnObject(g26,g8)
    c: Coincident(g30,g31)
    c: Coincident(g31,g32)
    c: Coincident(g32,g33)
    c: Coincident(g33,g30)
    c: Horizontal(g30)
    c: Horizontal(g32)
    c: Vertical(g31)
    c: Vertical(g33)
    c: PointOnObject(g30,g25)
    c: Equal(g2,g6)
    c: Equal(g6,g19)
    c: Equal(g19,g28)
    c: Equal(g28,g32)
    c: Equal(g32,g23)
    c: Equal(g23,g15)
    c: Equal(g15,g11)
    c: Equal(g5,g18)
    c: Equal(g18,g24)
    c: Equal(g24,g16)
    c: DistanceY(g7,g7) = 2.14
    c: Equal(g1,g12)
    c: Equal(g12,g33)
    c: Equal(g33,g27)
    c: Vertical(g34)
    c: Vertical(g35)
    c: Coincident(g36,g37)
    c: Coincident(g37,g38)
    c: Coincident(g38,g39)
    c: Coincident(g39,g36)
    c: Horizontal(g36)
    c: Horizontal(g38)
    c: Vertical(g37)
    c: Vertical(g39)
    c: PointOnObject(g36,g34)
    c: Coincident(g40,g41)
    c: Coincident(g41,g42)
    c: Coincident(g42,g43)
    c: Coincident(g43,g40)
    c: Horizontal(g40)
    c: Horizontal(g42)
    c: Vertical(g41)
    c: Vertical(g43)
    c: PointOnObject(g40,g34)
    c: Coincident(g44,g45)
    c: Coincident(g45,g46)
    c: Coincident(g46,g47)
    c: Coincident(g47,g44)
    c: Horizontal(g44)
    c: Horizontal(g46)
    c: Vertical(g45)
    c: Vertical(g47)
    c: PointOnObject(g44,g34)
    c: Coincident(g48,g49)
    c: Coincident(g49,g50)
    c: Coincident(g50,g51)
    c: Coincident(g51,g48)
    c: Horizontal(g48)
    c: Horizontal(g50)
    c: Vertical(g49)
    c: Vertical(g51)
    c: PointOnObject(g48,g35)
    c: Coincident(g52,g53)
    c: Coincident(g53,g54)
    c: Coincident(g54,g55)
    c: Coincident(g55,g52)
    c: Horizontal(g52)
    c: Horizontal(g54)
    c: Vertical(g53)
    c: Vertical(g55)
    c: PointOnObject(g52,g35)
    c: Coincident(g56,g57)
    c: Coincident(g57,g58)
    c: Coincident(g58,g59)
    c: Coincident(g59,g56)
    c: Horizontal(g56)
    c: Horizontal(g58)
    c: Vertical(g57)
    c: Vertical(g59)
    c: PointOnObject(g56,g35)
    c: DistanceX(g34,g8) = 1
    c: Equal(g38,g42)
    c: Equal(g42,g46)
    c: Equal(g46,g50)
    c: Equal(g50,g54)
    c: Equal(g54,g56)
    c: Equal(g41,g45)
    c: Equal(g45,g37)
    c: Equal(g37,g57)
    c: Equal(g57,g53)
    c: Equal(g53,g49)
    c: DistanceX(g50,g50) = 0.7
    c: DistanceY(g49,g49) = 1.3
    c: Coincident(g60,g4)
    c: Coincident(g60,g13)
    c: Horizontal(g60)
    c: Coincident(g61,g17)
    c: Coincident(g61,g21)
    c: Horizontal(g61)
    c: Coincident(g62,g26)
    c: Coincident(g62,g30)
    c: Horizontal(g62)
    c: DistanceY(g0,g26) = 6.58
    c: DistanceY(g10,g10) = 1.1
    c: Coincident(g63,g0)
    c: Coincident(g63,g9)
    c: Horizontal(g63)
    c: Coincident(g64,g36)
    c: Coincident(g64,g56)
    c: Coincident(g65,g40)
    c: Coincident(g65,g52)
    c: Coincident(g66,g44)
    c: Coincident(g66,g48)
    c: Horizontal(g66)
    c: Horizontal(g65)
    c: Horizontal(g64)
    c: DistanceY(g0,g36) = 0.65
    c: DistanceY(g0,g40) = 3.19
    c: DistanceY(g0,g44) = 5.73
    c: DistanceX(g0,g35) = 6.94
    c: Coincident(g67,g68)
    c: Coincident(g68,g69)
    c: Coincident(g69,g70)
    c: Coincident(g70,g67)
    c: Horizontal(g67)
    c: Horizontal(g69)
    c: Vertical(g68)
    c: Vertical(g70)
    c: Coincident(g71,g72)
    c: Coincident(g72,g73)
    c: Coincident(g73,g74)
    c: Coincident(g74,g71)
    c: Horizontal(g71)
    c: Horizontal(g73)
    c: Vertical(g72)
    c: Vertical(g74)
    c: Coincident(g75,g76)
    c: Coincident(g76,g77)
    c: Coincident(g77,g78)
    c: Coincident(g78,g75)
    c: Horizontal(g75)
    c: Horizontal(g77)
    c: Vertical(g76)
    c: Vertical(g78)
    c: Coincident(g79,g80)
    c: Coincident(g80,g81)
    c: Coincident(g81,g82)
    c: Coincident(g82,g79)
    c: Horizontal(g79)
    c: Horizontal(g81)
    c: Vertical(g80)
    c: Vertical(g82)
    c: Coincident(g83,g84)
    c: Coincident(g84,g85)
    c: Coincident(g85,g86)
    c: Coincident(g86,g83)
    c: Horizontal(g83)
    c: Horizontal(g85)
    c: Vertical(g84)
    c: Vertical(g86)
    c: Coincident(g87,g88)
    c: Coincident(g88,g89)
    c: Coincident(g89,g90)
    c: Coincident(g90,g87)
    c: Horizontal(g87)
    c: Horizontal(g89)
    c: Vertical(g88)
    c: Vertical(g90)
    c: Coincident(g91,g92)
    c: Coincident(g92,g93)
    c: Coincident(g93,g94)
    c: Coincident(g94,g91)
    c: Horizontal(g91)
    c: Horizontal(g93)
    c: Vertical(g92)
    c: Vertical(g94)
    c: Coincident(g95,g96)
    c: Coincident(g96,g97)
    c: Coincident(g97,g98)
    c: Coincident(g98,g95)
    c: Horizontal(g95)
    c: Horizontal(g97)
    c: Vertical(g96)
    c: Vertical(g98)
    c: Coincident(g99,g100)
    c: Coincident(g100,g101)
    c: Coincident(g101,g102)
    c: Coincident(g102,g99)
    c: Horizontal(g99)
    c: Horizontal(g101)
    c: Vertical(g100)
    c: Vertical(g102)
    c: Coincident(g103,g104)
    c: Coincident(g104,g105)
    c: Coincident(g105,g106)
    c: Coincident(g106,g103)
    c: Horizontal(g103)
    c: Horizontal(g105)
    c: Vertical(g104)
    c: Vertical(g106)
    c: Coincident(g107,g105)
    c: Vertical(g107)
    c: Coincident(g108,g97)
    c: Vertical(g108)
    c: Coincident(g109,g91)
    c: Vertical(g109)
    c: Equal(g67,g71)
    c: Equal(g71,g105)
    c: Equal(g105,g101)
    c: Equal(g100,g104)
    c: Equal(g104,g72)
    c: Equal(g72,g68)
    c: Equal(g96,g94)
    c: Equal(g94,g88)
    c: Equal(g88,g86)
    c: Equal(g86,g80)
    c: Equal(g80,g78)
    c: Equal(g77,g81)
    c: Equal(g81,g83)
    c: Equal(g83,g89)
    c: Equal(g89,g91)
    c: Equal(g91,g97)
    c: PointOnObject(g83,g109)
    c: PointOnObject(g77,g109)
    c: PointOnObject(g87,g108)
    c: PointOnObject(g79,g108)
    c: Coincident(g110,g101)
    c: Vertical(g110)
    c: PointOnObject(g71,g110)
    c: DistanceX(g103,g103) = 0.56
    c: DistanceX(g95,g95) = 0.75
    c: DistanceY(g96,g96) = 0.5
    c: PointOnObject(g67,g107)
    c: DistanceX(g0,g107) = 2.42
    c: DistanceX(g0,g108) = 2.53
    c: DistanceX(g0,g109) = 3.36
    c: DistanceX(g0,g110) = 3.66
    c: Coincident(g111,g104)
    c: Coincident(g111,g101)
    c: Coincident(g112,g67)
    c: Coincident(g112,g71)
    c: Horizontal(g112)
    c: Horizontal(g111)
    c: DistanceY(g0,g67) = 0.55
    c: DistanceY(g0,g105) = 6.79
    c: DistanceY(g100,g100) = 0.34
    c: DistanceY(g0,g77) = 1.03
    c: DistanceY(g0,g81) = 1.68
    c: DistanceY(g0,g83) = 2.77
    c: DistanceY(g0,g89) = 4.41
    c: DistanceY(g0,g91) = 5.5
    c: DistanceY(g0,g97) = 6.15
    c: Coincident(g113,g114)
    c: Coincident(g114,g115)
    c: Coincident(g115,g116)
    c: Coincident(g116,g113)
    c: Horizontal(g114)
    c: Horizontal(g116)
    c: Vertical(g113)
    c: Vertical(g115)
    c: Symmetric(g114,g113,g117)
    c: Coincident(g117,g-1)
    c: PointOnObject(g28,g114)
    c: PointOnObject(g46,g115)
    c: PointOnObject(g48,g113)
    c: PointOnObject(g9,g116)
